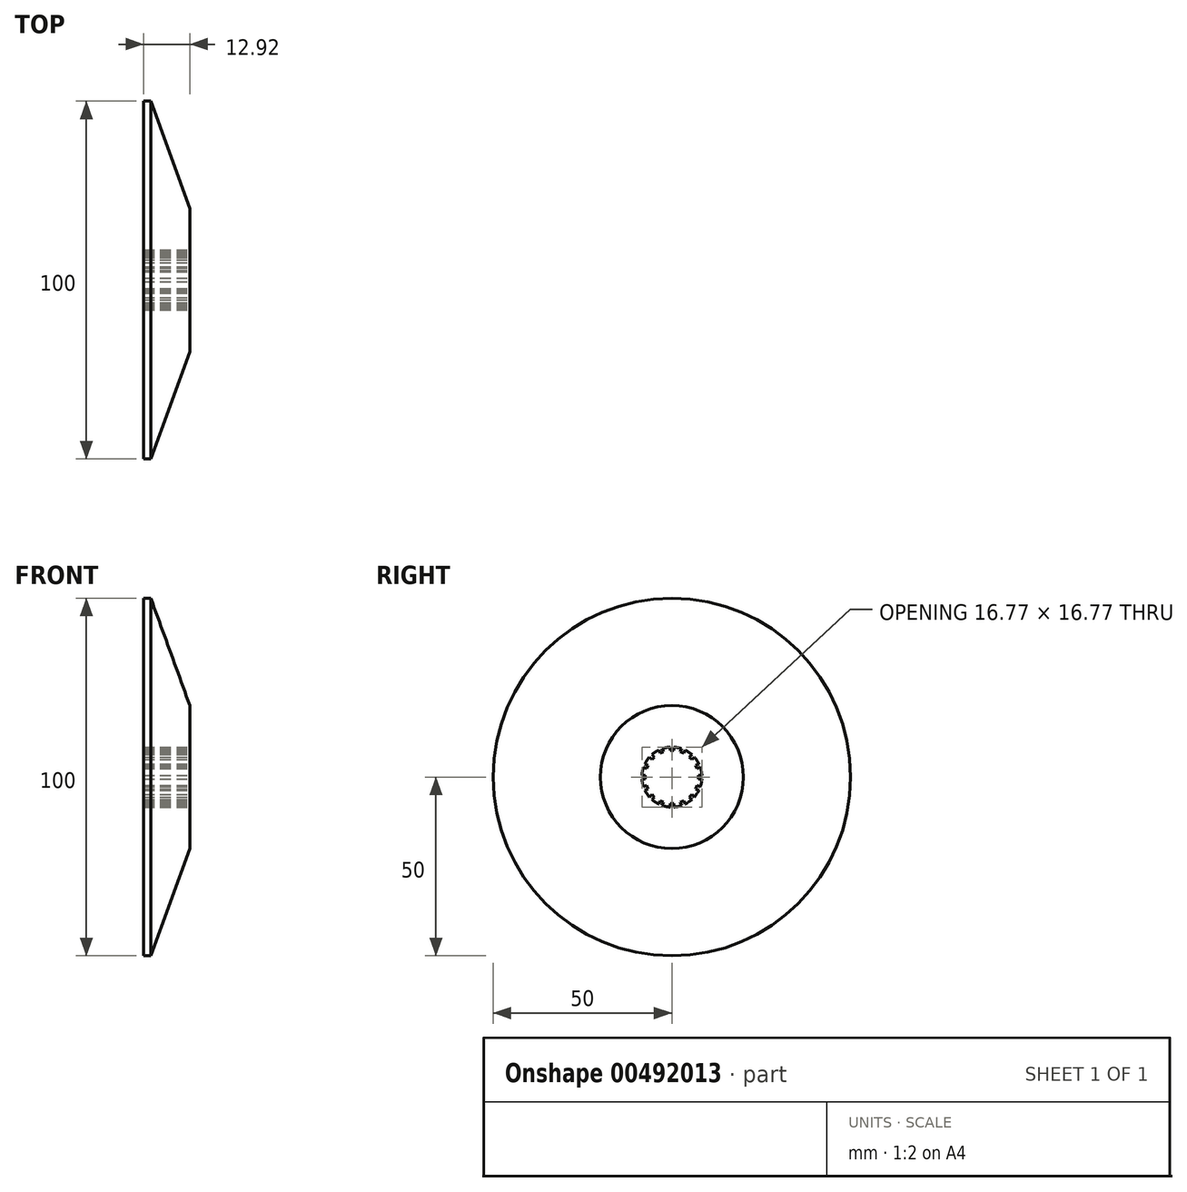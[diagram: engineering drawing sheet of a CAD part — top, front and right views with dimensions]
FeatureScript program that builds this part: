
annotation { "Feature Type Name" : "Feature", "Feature Type Description" : "" }
export const myFeature = defineFeature(function(context is Context, id is Id, definition is map)
    precondition{}
    {
        {
            var Q0;
            Q0=qCreatedBy(makeId("Front.planeOp"),FACE);
            var sketch = newSketch(context, id + "F0", { "sketchPlane" : qUnion([Q0])});
            skLineSegment(sketch, "E0", {"start": v(0, 0) * mm, "end": v(0, 20) * mm});
            skLineSegment(sketch, "E1", {"start": v(0, 20) * mm, "end": v(-10.92, 50) * mm});
            skLineSegment(sketch, "E2", {"start": v(-10.92, 50) * mm, "end": v(-12.92, 50) * mm});
            skLineSegment(sketch, "E3", {"start": v(-12.92, 50) * mm, "end": v(-12.92, 0) * mm});
            skLineSegment(sketch, "E4", {"start": v(-12.92, 0) * mm, "end": v(0, 0) * mm});
            skSolve(sketch);
        }
        {
            var Q0;
            Q0 = qSketchRegion(id + "F0", true);
            var Q1;
            Q1=sQuery(id+"F0.wireOp",EDGE,"E4");
            revolve(context, id + "F1", {"entities" : qUnion([Q0]), "axis" : qUnion([Q1]), "revolveType" : RevolveType.FULL});
        }
        {
            var Q0;
            Q0=qCreatedBy(makeId("Right.planeOp"),FACE);
            var sketch = newSketch(context, id + "F2", { "sketchPlane" : qUnion([Q0])});
            skPoint(sketch, "E5", {"position": v(0, 0) * mm});
            skSolve(sketch);
        }
        {
            var Q0;
            Q0=sQuery(id+"F2.wireOp",VERTEX,"E5");
            var Q1;
            Q1=makeQuery(id+"F1.opRevolve","SWEPT_BODY",BODY,{"disambiguationData":[OSD([sQuery(id+"F0.wireOp",EDGE,"E0"),sQuery(id+"F0.wireOp",EDGE,"E1"),sQuery(id+"F0.wireOp",EDGE,"E2"),sQuery(id+"F0.wireOp",EDGE,"E3"),sQuery(id+"F0.wireOp",EDGE,"E4")])]});
            hole(context, id + "F3", {"style" : HoleStyle.SIMPLE, "endStyle" : HoleEndStyle.THROUGH, "holeDiameter" : 16.8 * mm, "isTappedThrough" : true, "tappedDepth" : 12 * mm, "tapClearance" : 3, "locations" : qUnion([Q0]), "scope" : qUnion([Q1])});
        }
        {
            var Q0;
            Q0=qCreatedBy(makeId("Right.planeOp"),FACE);
            var sketch = newSketch(context, id + "F4", { "sketchPlane" : qUnion([Q0])});
            skArc(sketch, "E6", {"start": v(0.5, 8.39) * mm, "mid": v(0, 8.4) * mm, "end": v(-0.5, 8.39) * mm});
            skLineSegment(sketch, "E7.top", {"start": v(0.5, 7.4) * mm, "end": v(-0.5, 7.4) * mm});
            skLineSegment(sketch, "E7.left", {"start": v(0.5, 8.39) * mm, "end": v(0.5, 7.4) * mm});
            skLineSegment(sketch, "E7.right", {"start": v(-0.5, 8.39) * mm, "end": v(-0.5, 7.4) * mm});
            skPoint(sketch, "E7.middle", {"position": v(0, 8.4) * mm});
            skPoint(sketch, "E8.1.0", {"position": v(-3.21, 7.76) * mm});
            skArc(sketch, "E8.1.1", {"start": v(-2.75, 7.94) * mm, "mid": v(-3.21, 7.76) * mm, "end": v(-3.67, 7.56) * mm});
            skLineSegment(sketch, "E8.1.2", {"start": v(-2.37, 7.03) * mm, "end": v(-3.3, 6.65) * mm});
            skLineSegment(sketch, "E8.1.3", {"start": v(-2.75, 7.94) * mm, "end": v(-2.37, 7.03) * mm});
            skLineSegment(sketch, "E8.1.4", {"start": v(-3.67, 7.56) * mm, "end": v(-3.3, 6.65) * mm});
            skPoint(sketch, "E8.2.0", {"position": v(-5.94, 5.94) * mm});
            skArc(sketch, "E8.2.1", {"start": v(-5.58, 6.28) * mm, "mid": v(-5.94, 5.94) * mm, "end": v(-6.28, 5.58) * mm});
            skLineSegment(sketch, "E8.2.2", {"start": v(-4.88, 5.59) * mm, "end": v(-5.59, 4.88) * mm});
            skLineSegment(sketch, "E8.2.3", {"start": v(-5.58, 6.28) * mm, "end": v(-4.88, 5.59) * mm});
            skLineSegment(sketch, "E8.2.4", {"start": v(-6.28, 5.58) * mm, "end": v(-5.59, 4.88) * mm});
            skArc(sketch, "E9.1.3.0", {"start": v(-7.56, 3.67) * mm, "mid": v(-7.76, 3.21) * mm, "end": v(-7.94, 2.75) * mm});
            skLineSegment(sketch, "E9.5.3.0", {"start": v(-6.65, 3.3) * mm, "end": v(-7.03, 2.37) * mm});
            skPoint(sketch, "E9.7.3.0", {"position": v(-7.76, 3.21) * mm});
            skLineSegment(sketch, "E9.8.3.0", {"start": v(-7.56, 3.67) * mm, "end": v(-6.65, 3.3) * mm});
            skLineSegment(sketch, "E9.11.3.0", {"start": v(-7.94, 2.75) * mm, "end": v(-7.03, 2.37) * mm});
            skArc(sketch, "E9.1.4.0", {"start": v(-8.39, 0.5) * mm, "mid": v(-8.4, 0) * mm, "end": v(-8.39, -0.5) * mm});
            skLineSegment(sketch, "E9.5.4.0", {"start": v(-7.4, 0.5) * mm, "end": v(-7.4, -0.5) * mm});
            skPoint(sketch, "E9.7.4.0", {"position": v(-8.4, 0) * mm});
            skLineSegment(sketch, "E9.8.4.0", {"start": v(-8.39, 0.5) * mm, "end": v(-7.4, 0.5) * mm});
            skLineSegment(sketch, "E9.11.4.0", {"start": v(-8.39, -0.5) * mm, "end": v(-7.4, -0.5) * mm});
            skArc(sketch, "E9.1.5.0", {"start": v(-7.94, -2.75) * mm, "mid": v(-7.76, -3.21) * mm, "end": v(-7.56, -3.67) * mm});
            skLineSegment(sketch, "E9.5.5.0", {"start": v(-7.03, -2.37) * mm, "end": v(-6.65, -3.3) * mm});
            skPoint(sketch, "E9.7.5.0", {"position": v(-7.76, -3.21) * mm});
            skLineSegment(sketch, "E9.8.5.0", {"start": v(-7.94, -2.75) * mm, "end": v(-7.03, -2.37) * mm});
            skLineSegment(sketch, "E9.11.5.0", {"start": v(-7.56, -3.67) * mm, "end": v(-6.65, -3.3) * mm});
            skArc(sketch, "E9.1.6.0", {"start": v(-6.28, -5.58) * mm, "mid": v(-5.94, -5.94) * mm, "end": v(-5.58, -6.28) * mm});
            skLineSegment(sketch, "E9.5.6.0", {"start": v(-5.59, -4.88) * mm, "end": v(-4.88, -5.59) * mm});
            skPoint(sketch, "E9.7.6.0", {"position": v(-5.94, -5.94) * mm});
            skLineSegment(sketch, "E9.8.6.0", {"start": v(-6.28, -5.58) * mm, "end": v(-5.59, -4.88) * mm});
            skLineSegment(sketch, "E9.11.6.0", {"start": v(-5.58, -6.28) * mm, "end": v(-4.88, -5.59) * mm});
            skArc(sketch, "E9.1.7.0", {"start": v(-3.67, -7.56) * mm, "mid": v(-3.21, -7.76) * mm, "end": v(-2.75, -7.94) * mm});
            skLineSegment(sketch, "E9.5.7.0", {"start": v(-3.3, -6.65) * mm, "end": v(-2.37, -7.03) * mm});
            skPoint(sketch, "E9.7.7.0", {"position": v(-3.21, -7.76) * mm});
            skLineSegment(sketch, "E9.8.7.0", {"start": v(-3.67, -7.56) * mm, "end": v(-3.3, -6.65) * mm});
            skLineSegment(sketch, "E9.11.7.0", {"start": v(-2.75, -7.94) * mm, "end": v(-2.37, -7.03) * mm});
            skArc(sketch, "E10.1.8.0", {"start": v(-0.5, -8.39) * mm, "mid": v(0, -8.4) * mm, "end": v(0.5, -8.39) * mm});
            skLineSegment(sketch, "E10.5.8.0", {"start": v(-0.5, -7.4) * mm, "end": v(0.5, -7.4) * mm});
            skPoint(sketch, "E10.7.8.0", {"position": v(0, -8.4) * mm});
            skLineSegment(sketch, "E10.8.8.0", {"start": v(-0.5, -8.39) * mm, "end": v(-0.5, -7.4) * mm});
            skLineSegment(sketch, "E10.11.8.0", {"start": v(0.5, -8.39) * mm, "end": v(0.5, -7.4) * mm});
            skArc(sketch, "E10.1.9.0", {"start": v(2.75, -7.94) * mm, "mid": v(3.21, -7.76) * mm, "end": v(3.67, -7.56) * mm});
            skLineSegment(sketch, "E10.5.9.0", {"start": v(2.37, -7.03) * mm, "end": v(3.3, -6.65) * mm});
            skPoint(sketch, "E10.7.9.0", {"position": v(3.21, -7.76) * mm});
            skLineSegment(sketch, "E10.8.9.0", {"start": v(2.75, -7.94) * mm, "end": v(2.37, -7.03) * mm});
            skLineSegment(sketch, "E10.11.9.0", {"start": v(3.67, -7.56) * mm, "end": v(3.3, -6.65) * mm});
            skArc(sketch, "E10.1.10.0", {"start": v(5.58, -6.28) * mm, "mid": v(5.94, -5.94) * mm, "end": v(6.28, -5.58) * mm});
            skLineSegment(sketch, "E10.5.10.0", {"start": v(4.88, -5.59) * mm, "end": v(5.59, -4.88) * mm});
            skPoint(sketch, "E10.7.10.0", {"position": v(5.94, -5.94) * mm});
            skLineSegment(sketch, "E10.8.10.0", {"start": v(5.58, -6.28) * mm, "end": v(4.88, -5.59) * mm});
            skLineSegment(sketch, "E10.11.10.0", {"start": v(6.28, -5.58) * mm, "end": v(5.59, -4.88) * mm});
            skArc(sketch, "E10.1.11.0", {"start": v(7.56, -3.67) * mm, "mid": v(7.76, -3.21) * mm, "end": v(7.94, -2.75) * mm});
            skLineSegment(sketch, "E10.5.11.0", {"start": v(6.65, -3.3) * mm, "end": v(7.03, -2.37) * mm});
            skPoint(sketch, "E10.7.11.0", {"position": v(7.76, -3.21) * mm});
            skLineSegment(sketch, "E10.8.11.0", {"start": v(7.56, -3.67) * mm, "end": v(6.65, -3.3) * mm});
            skLineSegment(sketch, "E10.11.11.0", {"start": v(7.94, -2.75) * mm, "end": v(7.03, -2.37) * mm});
            skArc(sketch, "E10.1.12.0", {"start": v(8.39, -0.5) * mm, "mid": v(8.4, 0) * mm, "end": v(8.39, 0.5) * mm});
            skLineSegment(sketch, "E10.5.12.0", {"start": v(7.4, -0.5) * mm, "end": v(7.4, 0.5) * mm});
            skPoint(sketch, "E10.7.12.0", {"position": v(8.4, 0) * mm});
            skLineSegment(sketch, "E10.8.12.0", {"start": v(8.39, -0.5) * mm, "end": v(7.4, -0.5) * mm});
            skLineSegment(sketch, "E10.11.12.0", {"start": v(8.39, 0.5) * mm, "end": v(7.4, 0.5) * mm});
            skArc(sketch, "E10.1.13.0", {"start": v(7.94, 2.75) * mm, "mid": v(7.76, 3.21) * mm, "end": v(7.56, 3.67) * mm});
            skLineSegment(sketch, "E10.5.13.0", {"start": v(7.03, 2.37) * mm, "end": v(6.65, 3.3) * mm});
            skPoint(sketch, "E10.7.13.0", {"position": v(7.76, 3.21) * mm});
            skLineSegment(sketch, "E10.8.13.0", {"start": v(7.94, 2.75) * mm, "end": v(7.03, 2.37) * mm});
            skLineSegment(sketch, "E10.11.13.0", {"start": v(7.56, 3.67) * mm, "end": v(6.65, 3.3) * mm});
            skArc(sketch, "E10.1.14.0", {"start": v(6.28, 5.58) * mm, "mid": v(5.94, 5.94) * mm, "end": v(5.58, 6.28) * mm});
            skLineSegment(sketch, "E10.5.14.0", {"start": v(5.59, 4.88) * mm, "end": v(4.88, 5.59) * mm});
            skPoint(sketch, "E10.7.14.0", {"position": v(5.94, 5.94) * mm});
            skLineSegment(sketch, "E10.8.14.0", {"start": v(6.28, 5.58) * mm, "end": v(5.59, 4.88) * mm});
            skLineSegment(sketch, "E10.11.14.0", {"start": v(5.58, 6.28) * mm, "end": v(4.88, 5.59) * mm});
            skArc(sketch, "E10.1.15.0", {"start": v(3.67, 7.56) * mm, "mid": v(3.21, 7.76) * mm, "end": v(2.75, 7.94) * mm});
            skLineSegment(sketch, "E10.5.15.0", {"start": v(3.3, 6.65) * mm, "end": v(2.37, 7.03) * mm});
            skPoint(sketch, "E10.7.15.0", {"position": v(3.21, 7.76) * mm});
            skLineSegment(sketch, "E10.8.15.0", {"start": v(3.67, 7.56) * mm, "end": v(3.3, 6.65) * mm});
            skLineSegment(sketch, "E10.11.15.0", {"start": v(2.75, 7.94) * mm, "end": v(2.37, 7.03) * mm});
            skSolve(sketch);
        }
        {
            var Q0;
            Q0 = qSketchRegion(id + "F4", true);
            extrude(context, id + "F5", {"entities" : qUnion([Q0]), "operationType" : NewBodyOperationType.ADD, "oppositeDirection" : true, "depth" : 12.92 * mm});
        }
    });
